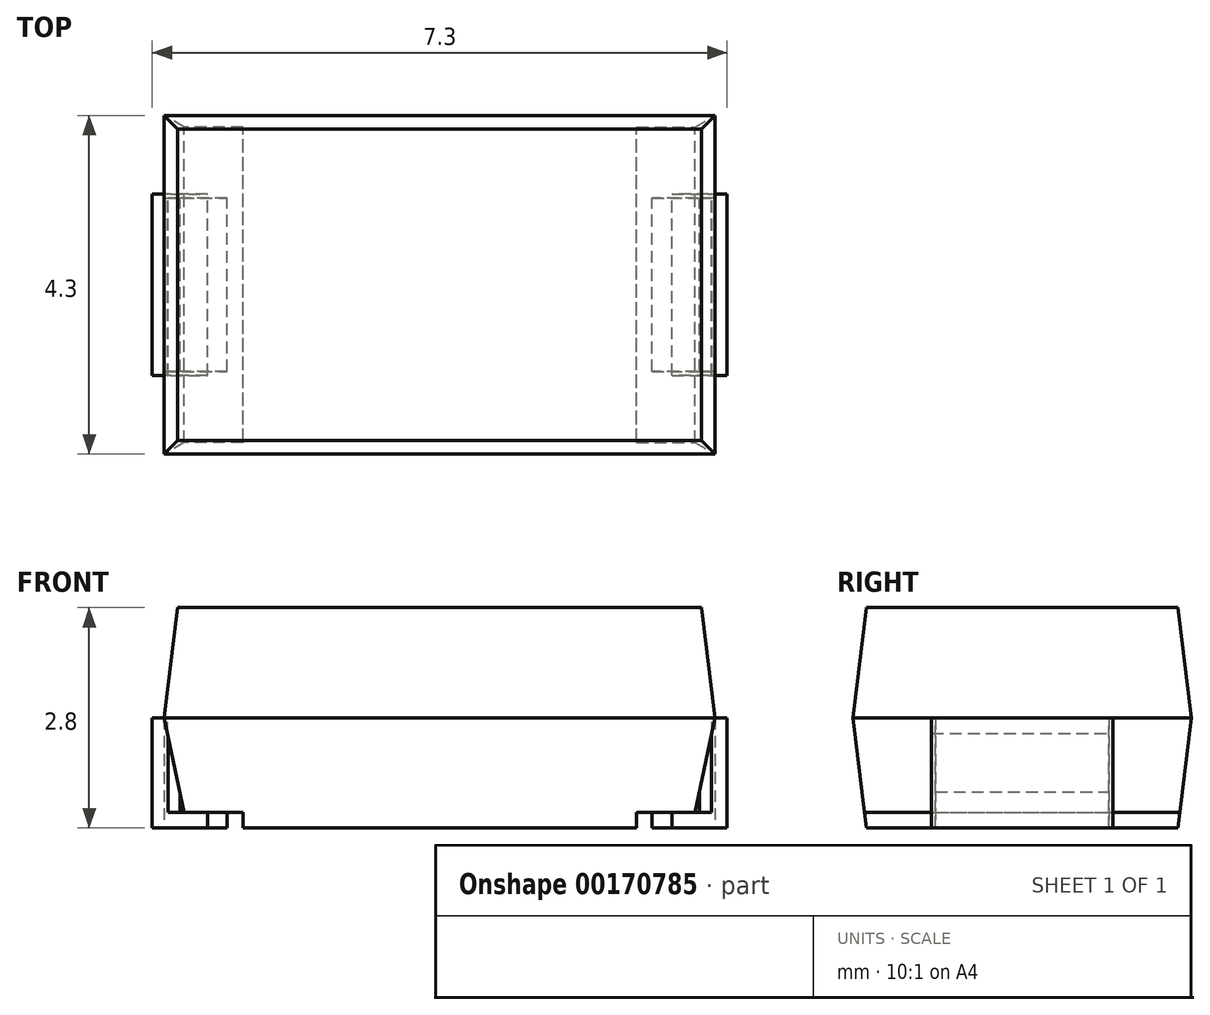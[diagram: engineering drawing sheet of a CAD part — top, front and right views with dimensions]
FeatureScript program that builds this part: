
annotation { "Feature Type Name" : "Feature", "Feature Type Description" : "" }
export const myFeature = defineFeature(function(context is Context, id is Id, definition is map)
    precondition{}
    {
        {
            assignVariable(context, id + "F0", {"variableType" : VariableType.LENGTH, "name" : "width", "lengthValue" : 4.3 * mm});
        }
        {
            var Q0;
            Q0=qCreatedBy(makeId("Front.planeOp"),FACE);
            var sketch = newSketch(context, id + "F1", { "sketchPlane" : qUnion([Q0])});
            skLineSegment(sketch, "E0", {"start": v(-2.5, 0) * mm, "end": v(-2.5, 0.2) * mm});
            skLineSegment(sketch, "E1", {"start": v(-2.5, 0.2) * mm, "end": v(-3.24, 0.2) * mm});
            skLineSegment(sketch, "E2", {"start": v(-3.24, 0.2) * mm, "end": v(-3.5, 1.4) * mm});
            skLineSegment(sketch, "E3", {"start": v(-3.5, 1.4) * mm, "end": v(-3.33, 2.8) * mm});
            skLineSegment(sketch, "E4", {"start": v(-3.5, 1.4) * mm, "end": v(-3.5, 0) * mm});
            skLineSegment(sketch, "E5", {"start": v(-3.5, 0) * mm, "end": v(-2.7, 0) * mm});
            skLineSegment(sketch, "E6", {"start": v(-2.7, 0) * mm, "end": v(-2.7, 0.2) * mm});
            skLineSegment(sketch, "E7", {"start": v(-2.7, 0.2) * mm, "end": v(-3.3, 0.2) * mm});
            skLineSegment(sketch, "E8", {"start": v(-3.3, 0.2) * mm, "end": v(-3.3, 0.46) * mm});
            skLineSegment(sketch, "E9.MirrorCS", {"start": v(2.7, 0) * mm, "end": v(2.7, 0.2) * mm});
            skLineSegment(sketch, "E10.MirrorCS", {"start": v(2.5, 0) * mm, "end": v(2.5, 0.2) * mm});
            skLineSegment(sketch, "E11.MirrorCS", {"start": v(3.5, 1.4) * mm, "end": v(3.5, 0) * mm});
            skLineSegment(sketch, "E12.MirrorCS", {"start": v(3.5, 1.4) * mm, "end": v(3.33, 2.8) * mm});
            skLineSegment(sketch, "E13.MirrorCS", {"start": v(3.5, 0) * mm, "end": v(2.7, 0) * mm});
            skLineSegment(sketch, "E14.MirrorCS", {"start": v(3.3, 0.2) * mm, "end": v(3.3, 0.46) * mm});
            skLineSegment(sketch, "E15.MirrorCS", {"start": v(2.7, 0.2) * mm, "end": v(3.3, 0.2) * mm});
            skLineSegment(sketch, "E16.MirrorCS", {"start": v(3.24, 0.2) * mm, "end": v(3.5, 1.4) * mm});
            skLineSegment(sketch, "E17.MirrorCS", {"start": v(2.5, 0.2) * mm, "end": v(3.24, 0.2) * mm});
            skLineSegment(sketch, "E18", {"start": v(-3.33, 2.8) * mm, "end": v(3.33, 2.8) * mm});
            skLineSegment(sketch, "E19", {"start": v(2.5, 0) * mm, "end": v(-2.5, 0) * mm});
            skLineSegment(sketch, "E20", {"start": v(-3.3, 0.2) * mm, "end": v(-3.5, 0.2) * mm, "construction": true});
            skSolve(sketch);
        }
        {
            var Q0;
            Q0=makeQuery(id+"F1.imprint","IMPRINT",FACE,{"disambiguationData":[TD([[makeQuery(id+"F1.imprint","IMPRINT",EDGE,{"derivedFrom":sQuery(id+"F1.wireOp",EDGE,"E0")}),-1.0]])]});
            extrude(context, id + "F2", {"entities" : qUnion([Q0]), "depth" : getVariable(context, 'width'), "offsetDistance" : 25 * mm, "symmetric" : true});
        }
        {
            var Q0;
            Q0=qCreatedBy(makeId("Right.planeOp"),FACE);
            var sketch = newSketch(context, id + "F3", { "sketchPlane" : qUnion([Q0])});
            skLineSegment(sketch, "E21", {"start": v(-2.15, 2.8) * mm, "end": v(-1.98, 2.8) * mm});
            skLineSegment(sketch, "E22", {"start": v(-1.98, 2.8) * mm, "end": v(-2.15, 1.4) * mm});
            skLineSegment(sketch, "E23", {"start": v(-2.15, 1.4) * mm, "end": v(-1.98, 0) * mm});
            skLineSegment(sketch, "E24", {"start": v(-1.98, 0) * mm, "end": v(-2.15, 0) * mm});
            skLineSegment(sketch, "E25", {"start": v(-2.15, 0) * mm, "end": v(-2.15, 2.8) * mm});
            skLineSegment(sketch, "E26.MirrorCS", {"start": v(2.15, 1.4) * mm, "end": v(1.98, 0) * mm});
            skLineSegment(sketch, "E27.MirrorCS", {"start": v(2.15, 0) * mm, "end": v(2.15, 2.8) * mm});
            skLineSegment(sketch, "E28.MirrorCS", {"start": v(1.98, 2.8) * mm, "end": v(2.15, 1.4) * mm});
            skLineSegment(sketch, "E29.MirrorCS", {"start": v(1.98, 0) * mm, "end": v(2.15, 0) * mm});
            skLineSegment(sketch, "E30.MirrorCS", {"start": v(2.15, 2.8) * mm, "end": v(1.98, 2.8) * mm});
            skSolve(sketch);
        }
        {
            var Q0;
            Q0 = qSketchRegion(id + "F3", true);
            extrude(context, id + "F4", {"entities" : qUnion([Q0]), "operationType" : NewBodyOperationType.REMOVE, "endBound" : BoundingType.THROUGH_ALL, "oppositeDirection" : true, "depth" : 25 * mm, "offsetDistance" : 25 * mm, "hasSecondDirection" : true, "secondDirectionBound" : BoundingType.THROUGH_ALL, "secondDirectionOppositeDirection" : false, "secondDirectionDepth" : 25 * mm});
        }
        {
            var Q0;
            Q0=qCreatedBy(makeId("Front.planeOp"),FACE);
            var sketch = newSketch(context, id + "F5", { "sketchPlane" : qUnion([Q0])});
            skLineSegment(sketch, "E31", {"start": v(-3.46, 1.4) * mm, "end": v(-3.65, 1.4) * mm});
            skLineSegment(sketch, "E32", {"start": v(-3.65, 1.4) * mm, "end": v(-3.65, 0) * mm});
            skLineSegment(sketch, "E33", {"start": v(-3.65, 0) * mm, "end": v(-2.95, 0) * mm});
            skLineSegment(sketch, "E34", {"start": v(-2.95, 0) * mm, "end": v(-2.95, 0.2) * mm});
            skLineSegment(sketch, "E35", {"start": v(-2.95, 0.2) * mm, "end": v(-3.45, 0.2) * mm});
            skLineSegment(sketch, "E36", {"start": v(-3.45, 0.2) * mm, "end": v(-3.45, 1.2) * mm});
            skLineSegment(sketch, "E37", {"start": v(-3.46, 1.2) * mm, "end": v(-3.45, 1.2) * mm});
            skLineSegment(sketch, "E38", {"start": v(-3.46, 1.2) * mm, "end": v(-3.46, 1.4) * mm});
            skLineSegment(sketch, "E39", {"start": v(-3.45, 1.2) * mm, "end": v(-3.65, 1.2) * mm, "construction": true});
            skLineSegment(sketch, "E40.MirrorCS", {"start": v(3.46, 1.2) * mm, "end": v(3.46, 1.4) * mm});
            skLineSegment(sketch, "E41.MirrorCS", {"start": v(3.46, 1.4) * mm, "end": v(3.65, 1.4) * mm});
            skLineSegment(sketch, "E42.MirrorCS", {"start": v(3.65, 1.4) * mm, "end": v(3.65, 0) * mm});
            skLineSegment(sketch, "E43.MirrorCS", {"start": v(3.45, 0.2) * mm, "end": v(3.45, 1.2) * mm});
            skLineSegment(sketch, "E44.MirrorCS", {"start": v(3.46, 1.2) * mm, "end": v(3.45, 1.2) * mm});
            skLineSegment(sketch, "E45.MirrorCS", {"start": v(2.95, 0.2) * mm, "end": v(3.45, 0.2) * mm});
            skLineSegment(sketch, "E46.MirrorCS", {"start": v(3.65, 0) * mm, "end": v(2.95, 0) * mm});
            skLineSegment(sketch, "E47.MirrorCS", {"start": v(2.95, 0) * mm, "end": v(2.95, 0.2) * mm});
            skSolve(sketch);
        }
        {
            var Q0;
            Q0 = qSketchRegion(id + "F5", true);
            extrude(context, id + "F6", {"entities" : qUnion([Q0]), "flatOperationType" : FlatOperationType.REMOVE, "depth" : getVariable(context, 'width') - 2 * mm, "offsetDistance" : 25 * mm, "domain" : OperationDomain.MODEL, "symmetric" : true});
        }
        {
            var Q0;
            {var subQ1=sQuery(id+"F1.wireOp",EDGE,"E4");Q0=makeQuery(id+"F1.imprint","IMPRINT",FACE,{"disambiguationData":[TD([[makeQuery(id+"F1.imprint","IMPRINT",EDGE,{"derivedFrom":subQ1}),1.0]])]});}
            var Q1;
            {var subQ2=sQuery(id+"F1.wireOp",EDGE,"E9.MirrorCS");Q1=makeQuery(id+"F1.imprint","IMPRINT",FACE,{"disambiguationData":[TD([[makeQuery(id+"F1.imprint","IMPRINT",EDGE,{"derivedFrom":subQ2}),-1.0]])]});}
            extrude(context, id + "F7", {"entities" : qUnion([Q0, Q1]), "depth" : 2.2 * mm, "offsetDistance" : 25 * mm, "symmetric" : true});
        }
    });
